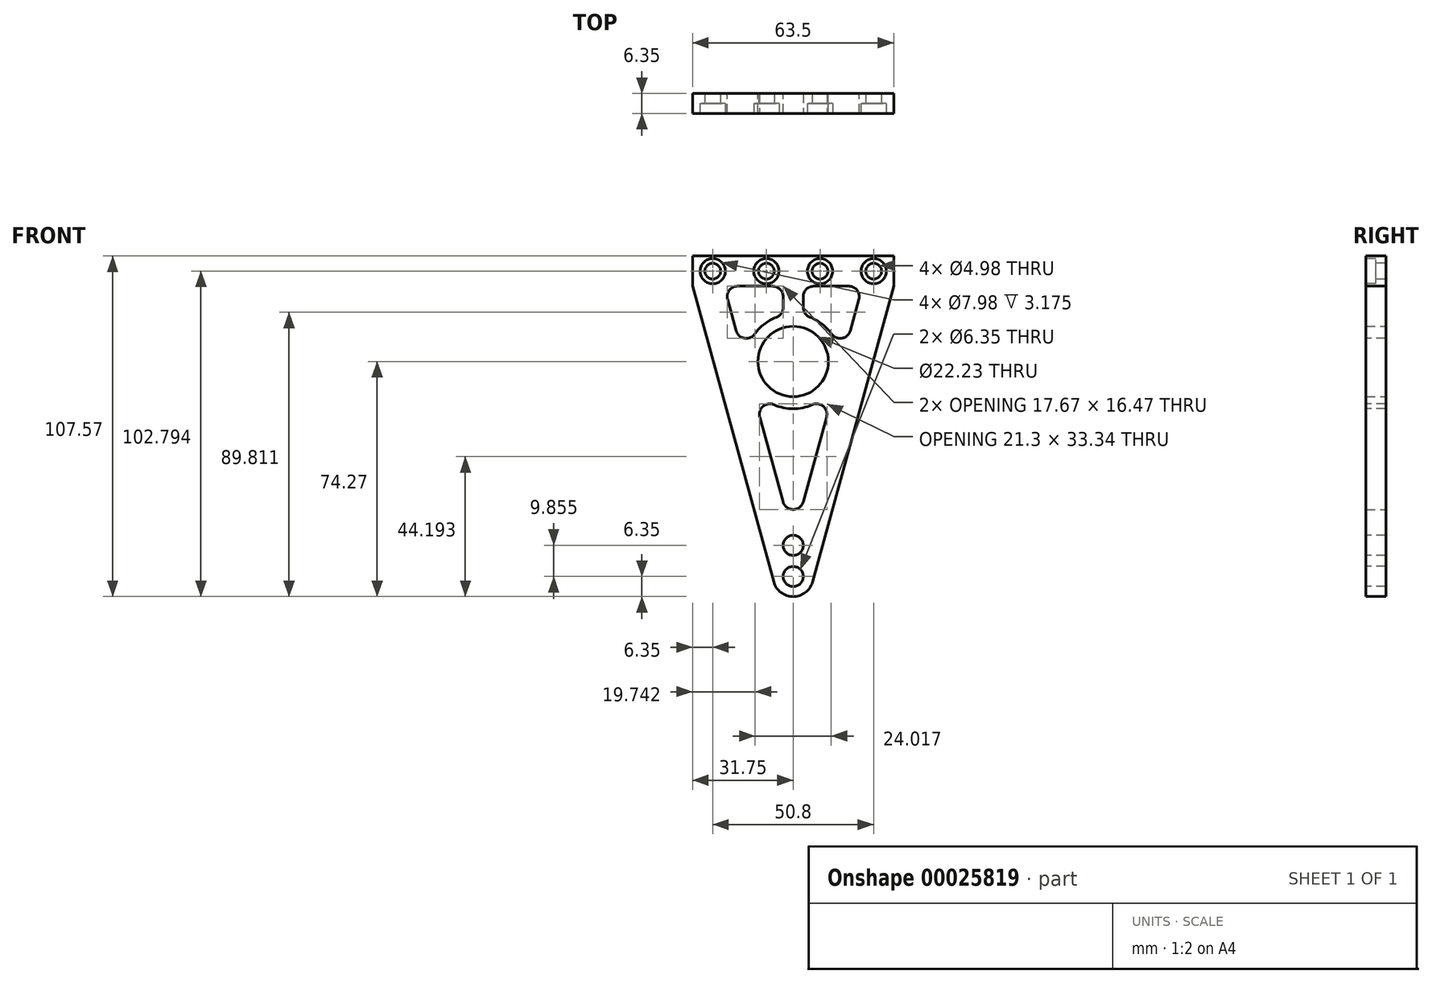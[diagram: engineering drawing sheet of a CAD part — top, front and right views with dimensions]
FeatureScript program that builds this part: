
annotation { "Feature Type Name" : "Feature", "Feature Type Description" : "" }
export const myFeature = defineFeature(function(context is Context, id is Id, definition is map)
    precondition{}
    {
        {
            var Q0;
            Q0=qCreatedBy(makeId("Front.planeOp"),FACE);
            var sketch = newSketch(context, id + "F0", { "sketchPlane" : qUnion([Q0])});
            skCircle(sketch, "E0", {"center": v(0, 0) * mm, "radius": 11.11 * mm});
            skLineSegment(sketch, "E1", {"start": v(0, 54.86) * mm, "end": v(0, 0) * mm, "construction": true});
            skLineSegment(sketch, "E2", {"start": v(0, 0) * mm, "end": v(80.81, 0) * mm, "construction": true});
            skLineSegment(sketch, "E3.bottom", {"start": v(-31.75, 33.3) * mm, "end": v(31.75, 33.3) * mm});
            skLineSegment(sketch, "E3.left", {"start": v(-31.75, 33.3) * mm, "end": v(-31.75, 23.77) * mm});
            skLineSegment(sketch, "E3.right", {"start": v(31.75, 33.3) * mm, "end": v(31.75, 23.77) * mm});
            skLineSegment(sketch, "E4", {"start": v(-31.75, 23.77) * mm, "end": v(-6.12, -69.6) * mm});
            skLineSegment(sketch, "E5", {"start": v(6.12, -69.6) * mm, "end": v(31.75, 23.77) * mm});
            skArc(sketch, "E6", {"start": v(-6.12, -69.6) * mm, "mid": v(0, -74.27) * mm, "end": v(6.12, -69.6) * mm});
            skSolve(sketch);
        }
        {
            var Q0;
            Q0=makeQuery(id+"F0.imprint","IMPRINT",FACE,{"disambiguationData":[TD([[makeQuery(id+"F0.imprint","IMPRINT",EDGE,{"derivedFrom":sQuery(id+"F0.wireOp",EDGE,"E0")}),-1.0]])]});
            extrude(context, id + "F1", {"entities" : qUnion([Q0]), "depth" : 6.35 * mm});
        }
        {
            var Q0;
            Q0=makeQuery(id+"F1.opExtrude","CAP_FACE",FACE,{"disambiguationData":[OSD([sQuery(id+"F0.wireOp",EDGE,"E0"),sQuery(id+"F0.wireOp",EDGE,"E3.bottom"),sQuery(id+"F0.wireOp",EDGE,"E3.left"),sQuery(id+"F0.wireOp",EDGE,"E3.right"),sQuery(id+"F0.wireOp",EDGE,"E4"),sQuery(id+"F0.wireOp",EDGE,"E5"),sQuery(id+"F0.wireOp",EDGE,"E6")])],"isStart":false});
            var sketch = newSketch(context, id + "F2", { "sketchPlane" : qUnion([Q0])});
            skLineSegment(sketch, "E7.0", {"start": v(21.87, 23.77) * mm, "end": v(3.17, 23.77) * mm});
            skLineSegment(sketch, "E7.1", {"start": v(0, -55.92) * mm, "end": v(13.77, -5.75) * mm});
            skLineSegment(sketch, "E7.2", {"start": v(-21.87, 23.77) * mm, "end": v(-14.78, -2.08) * mm});
            skArc(sketch, "E8", {"start": v(-13.77, -5.75) * mm, "mid": v(0, -14.92) * mm, "end": v(13.77, -5.75) * mm});
            skLineSegment(sketch, "E9.trimOffspring", {"start": v(-13.77, -5.75) * mm, "end": v(0, -55.92) * mm});
            skArc(sketch, "E10.trimOffspring", {"start": v(14.78, -2.08) * mm, "mid": v(12.25, 8.53) * mm, "end": v(3.18, 14.58) * mm});
            skLineSegment(sketch, "E11.trimOffspring", {"start": v(14.78, -2.08) * mm, "end": v(21.87, 23.77) * mm});
            skLineSegment(sketch, "E12", {"start": v(0, 0) * mm, "end": v(0, 52.94) * mm, "construction": true});
            skLineSegment(sketch, "E13", {"start": v(-3.17, 23.77) * mm, "end": v(-3.18, 14.58) * mm});
            skLineSegment(sketch, "E14", {"start": v(3.17, 23.77) * mm, "end": v(3.18, 14.58) * mm});
            skArc(sketch, "E15.trimOffspring", {"start": v(-3.18, 14.58) * mm, "mid": v(-12.25, 8.53) * mm, "end": v(-14.78, -2.08) * mm});
            skLineSegment(sketch, "E16.trimOffspring", {"start": v(-3.17, 23.77) * mm, "end": v(-21.87, 23.77) * mm});
            skSolve(sketch);
        }
        {
            var Q0;
            Q0=makeQuery(id+"F2.imprint","IMPRINT",FACE,{"disambiguationData":[TD([[makeQuery(id+"F2.imprint","IMPRINT",EDGE,{"derivedFrom":sQuery(id+"F2.wireOp",EDGE,"E7.2")}),1.0]])]});
            var Q1;
            Q1=makeQuery(id+"F2.imprint","IMPRINT",FACE,{"disambiguationData":[TD([[makeQuery(id+"F2.imprint","IMPRINT",EDGE,{"derivedFrom":sQuery(id+"F2.wireOp",EDGE,"E7.0")}),1.0]])]});
            var Q2;
            Q2=makeQuery(id+"F2.imprint","IMPRINT",FACE,{"disambiguationData":[TD([[makeQuery(id+"F2.imprint","IMPRINT",EDGE,{"derivedFrom":sQuery(id+"F2.wireOp",EDGE,"E7.1")}),1.0]])]});
            extrude(context, id + "F3", {"entities" : qUnion([Q0, Q1, Q2]), "operationType" : NewBodyOperationType.REMOVE, "endBound" : BoundingType.THROUGH_ALL, "oppositeDirection" : true, "depth" : 25.4 * mm});
        }
        {
            var Q0;
            Q0=makeQuery(id+"F3.boolean.opBoolean","COPY",EDGE,{"derivedFrom":makeQuery(id+"F3.opExtrude","SWEPT_EDGE",EDGE,{"disambiguationData":[OSD([sQuery(id+"F2.wireOp",EDGE,"E7.2"),sQuery(id+"F2.wireOp",EDGE,"E15.trimOffspring")])]})});
            var Q1;
            Q1=makeQuery(id+"F3.boolean.opBoolean","COPY",EDGE,{"derivedFrom":makeQuery(id+"F3.opExtrude","SWEPT_EDGE",EDGE,{"disambiguationData":[OSD([sQuery(id+"F2.wireOp",EDGE,"E7.1"),sQuery(id+"F2.wireOp",EDGE,"E9.trimOffspring")])]})});
            var Q2;
            Q2=makeQuery(id+"F3.boolean.opBoolean","COPY",EDGE,{"derivedFrom":makeQuery(id+"F3.opExtrude","SWEPT_EDGE",EDGE,{"disambiguationData":[OSD([sQuery(id+"F2.wireOp",EDGE,"E7.1"),sQuery(id+"F2.wireOp",EDGE,"E8")])]})});
            var Q3;
            Q3=makeQuery(id+"F3.boolean.opBoolean","COPY",EDGE,{"derivedFrom":makeQuery(id+"F3.opExtrude","SWEPT_EDGE",EDGE,{"disambiguationData":[OSD([sQuery(id+"F2.wireOp",EDGE,"E8"),sQuery(id+"F2.wireOp",EDGE,"E9.trimOffspring")])]})});
            var Q4;
            Q4=makeQuery(id+"F3.boolean.opBoolean","COPY",EDGE,{"derivedFrom":makeQuery(id+"F3.opExtrude","SWEPT_EDGE",EDGE,{"disambiguationData":[OSD([sQuery(id+"F2.wireOp",EDGE,"E7.0"),sQuery(id+"F2.wireOp",EDGE,"E14")])]})});
            var Q5;
            Q5=makeQuery(id+"F3.boolean.opBoolean","COPY",EDGE,{"derivedFrom":makeQuery(id+"F3.opExtrude","SWEPT_EDGE",EDGE,{"disambiguationData":[OSD([sQuery(id+"F2.wireOp",EDGE,"E13"),sQuery(id+"F2.wireOp",EDGE,"E16.trimOffspring")])]})});
            var Q6;
            Q6=makeQuery(id+"F3.boolean.opBoolean","COPY",EDGE,{"derivedFrom":makeQuery(id+"F3.opExtrude","SWEPT_EDGE",EDGE,{"disambiguationData":[OSD([sQuery(id+"F2.wireOp",EDGE,"E7.0"),sQuery(id+"F2.wireOp",EDGE,"E11.trimOffspring")])]})});
            var Q7;
            Q7=makeQuery(id+"F3.boolean.opBoolean","COPY",EDGE,{"derivedFrom":makeQuery(id+"F3.opExtrude","SWEPT_EDGE",EDGE,{"disambiguationData":[OSD([sQuery(id+"F2.wireOp",EDGE,"E7.2"),sQuery(id+"F2.wireOp",EDGE,"E16.trimOffspring")])]})});
            var Q8;
            Q8=makeQuery(id+"F3.boolean.opBoolean","COPY",EDGE,{"derivedFrom":makeQuery(id+"F3.opExtrude","SWEPT_EDGE",EDGE,{"disambiguationData":[OSD([sQuery(id+"F2.wireOp",EDGE,"E10.trimOffspring"),sQuery(id+"F2.wireOp",EDGE,"E11.trimOffspring")])]})});
            var Q9;
            Q9=makeQuery(id+"F3.boolean.opBoolean","COPY",EDGE,{"derivedFrom":makeQuery(id+"F3.opExtrude","SWEPT_EDGE",EDGE,{"disambiguationData":[OSD([sQuery(id+"F2.wireOp",EDGE,"E10.trimOffspring"),sQuery(id+"F2.wireOp",EDGE,"E14")])]})});
            var Q10;
            Q10=makeQuery(id+"F3.boolean.opBoolean","COPY",EDGE,{"derivedFrom":makeQuery(id+"F3.opExtrude","SWEPT_EDGE",EDGE,{"disambiguationData":[OSD([sQuery(id+"F2.wireOp",EDGE,"E13"),sQuery(id+"F2.wireOp",EDGE,"E15.trimOffspring")])]})});
            fillet(context, id + "F4", {"entities" : qUnion([Q0, Q1, Q2, Q3, Q4, Q5, Q6, Q7, Q8, Q9, Q10]), "radius" : 3.3 * mm, "tangentPropagation" : true, "allowEdgeOverflow" : false});
        }
        {
            var Q0;
            Q0=makeQuery(id+"F1.opExtrude","CAP_FACE",FACE,{"disambiguationData":[OSD([sQuery(id+"F0.wireOp",EDGE,"E0"),sQuery(id+"F0.wireOp",EDGE,"E3.bottom"),sQuery(id+"F0.wireOp",EDGE,"E3.left"),sQuery(id+"F0.wireOp",EDGE,"E3.right"),sQuery(id+"F0.wireOp",EDGE,"E4"),sQuery(id+"F0.wireOp",EDGE,"E5"),sQuery(id+"F0.wireOp",EDGE,"E6")])],"isStart":false});
            var sketch = newSketch(context, id + "F5", { "sketchPlane" : qUnion([Q0])});
            skLineSegment(sketch, "E17", {"start": v(-25.4, 28.52) * mm, "end": v(25.4, 28.52) * mm});
            skLineSegment(sketch, "E18", {"start": v(0, -67.92) * mm, "end": v(0, 28.52) * mm});
            skPoint(sketch, "E19", {"position": v(-8.47, 28.52) * mm});
            skPoint(sketch, "E20", {"position": v(8.47, 28.52) * mm});
            skPoint(sketch, "E21", {"position": v(0, -58.06) * mm});
            skSolve(sketch);
        }
        {
            var Q0;
            Q0=sQuery(id+"F5.wireOp",VERTEX,"E17.end");
            var Q1;
            Q1=sQuery(id+"F5.wireOp",VERTEX,"E20");
            var Q2;
            Q2=sQuery(id+"F5.wireOp",VERTEX,"E19");
            var Q3;
            Q3=sQuery(id+"F5.wireOp",VERTEX,"E17.start");
            var Q4;
            Q4=makeQuery(id+"F1.opExtrude","SWEPT_BODY",BODY,{"disambiguationData":[OSD([sQuery(id+"F0.wireOp",EDGE,"E0"),sQuery(id+"F0.wireOp",EDGE,"E3.bottom"),sQuery(id+"F0.wireOp",EDGE,"E3.left"),sQuery(id+"F0.wireOp",EDGE,"E3.right"),sQuery(id+"F0.wireOp",EDGE,"E4"),sQuery(id+"F0.wireOp",EDGE,"E5"),sQuery(id+"F0.wireOp",EDGE,"E6")])]});
            hole(context, id + "F6", {"style" : HoleStyle.C_BORE, "holeDiameter" : 4.98 * mm, "cBoreDiameter" : 7.98 * mm, "cBoreDepth" : 3.17 * mm, "endStyle" : HoleEndStyle.THROUGH, "locations" : qUnion([Q0, Q1, Q2, Q3]), "scope" : qUnion([Q4])});
        }
        {
            var Q0;
            Q0=sQuery(id+"F5.wireOp",VERTEX,"E21");
            var Q1;
            Q1=sQuery(id+"F5.wireOp",VERTEX,"E18.start");
            var Q2;
            Q2=makeQuery(id+"F1.opExtrude","SWEPT_BODY",BODY,{"disambiguationData":[OSD([sQuery(id+"F0.wireOp",EDGE,"E0"),sQuery(id+"F0.wireOp",EDGE,"E3.bottom"),sQuery(id+"F0.wireOp",EDGE,"E3.left"),sQuery(id+"F0.wireOp",EDGE,"E3.right"),sQuery(id+"F0.wireOp",EDGE,"E4"),sQuery(id+"F0.wireOp",EDGE,"E5"),sQuery(id+"F0.wireOp",EDGE,"E6")])]});
            hole(context, id + "F7", {"style" : HoleStyle.SIMPLE, "holeDiameter" : 6.35 * mm, "endStyle" : HoleEndStyle.THROUGH, "locations" : qUnion([Q0, Q1]), "scope" : qUnion([Q2])});
        }
    });
